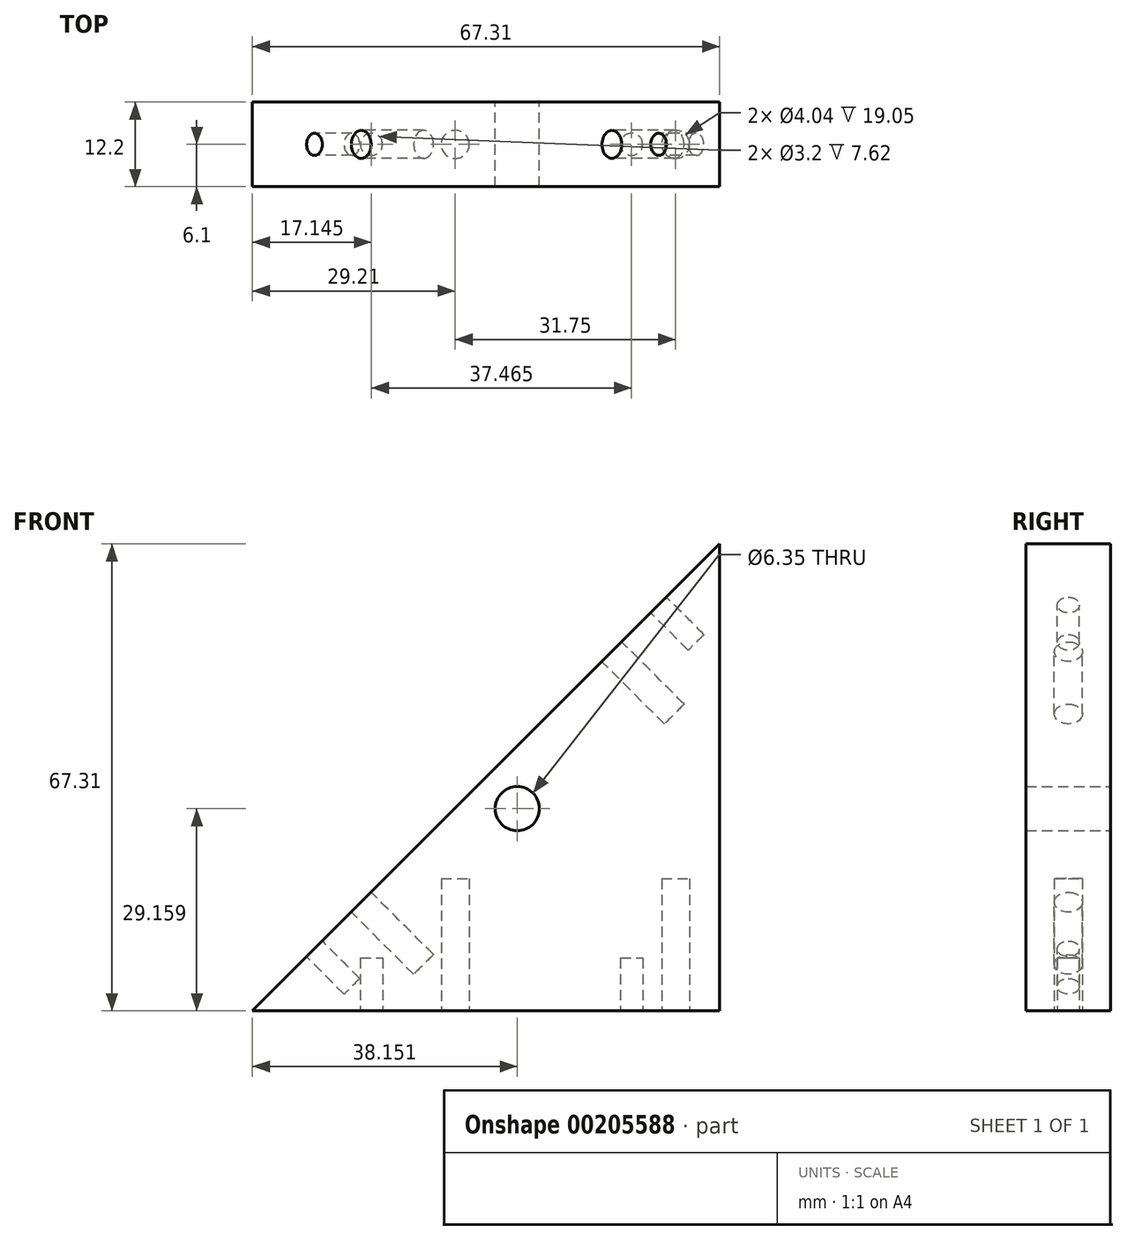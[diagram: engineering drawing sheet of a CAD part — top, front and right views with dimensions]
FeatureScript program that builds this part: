
annotation { "Feature Type Name" : "Feature", "Feature Type Description" : "" }
export const myFeature = defineFeature(function(context is Context, id is Id, definition is map)
    precondition{}
    {
        {
            var Q0;
            Q0=qCreatedBy(makeId("Front.planeOp"),FACE);
            var sketch = newSketch(context, id + "F0", { "sketchPlane" : qUnion([Q0])});
            skLineSegment(sketch, "E0", {"start": v(0, 0) * mm, "end": v(0, 67.31) * mm});
            skLineSegment(sketch, "E1", {"start": v(0, 67.31) * mm, "end": v(-67.31, 0) * mm});
            skLineSegment(sketch, "E2", {"start": v(-67.31, 0) * mm, "end": v(0, 0) * mm});
            skCircle(sketch, "E3", {"center": v(-29.16, 29.16) * mm, "radius": 3.18 * mm});
            skSolve(sketch);
        }
        {
            var Q0;
            Q0=qSketchRegion(id+"F0",true);
            extrude(context, id + "F1", {"entities" : qUnion([Q0]), "depth" : 12.2 * mm, "symmetric" : true});
        }
        {
            var Q0;
            Q0=makeQuery(id+"F1.opExtrude","SWEPT_FACE",FACE,{"disambiguationData":[OSD([sQuery(id+"F0.wireOp",EDGE,"E1")])]});
            var sketch = newSketch(context, id + "F2", { "sketchPlane" : qUnion([Q0])});
            skCircle(sketch, "E4", {"center": v(0, 35.15) * mm, "radius": 1.6 * mm});
            skCircle(sketch, "E5", {"center": v(0, -34.95) * mm, "radius": 1.6 * mm});
            skSolve(sketch);
        }
        {
            var Q0;
            Q0=qSketchRegion(id+"F2",true);
            extrude(context, id + "F3", {"entities" : qUnion([Q0]), "operationType" : NewBodyOperationType.REMOVE, "oppositeDirection" : true, "depth" : 7.62 * mm});
        }
        {
            var Q0;
            Q0=makeQuery(id+"F1.opExtrude","SWEPT_FACE",FACE,{"disambiguationData":[OSD([sQuery(id+"F0.wireOp",EDGE,"E1")])]});
            var sketch = newSketch(context, id + "F4", { "sketchPlane" : qUnion([Q0])});
            skCircle(sketch, "E6", {"center": v(0, 25.62) * mm, "radius": 2.02 * mm});
            skCircle(sketch, "E7", {"center": v(0, -25.43) * mm, "radius": 2.02 * mm});
            skSolve(sketch);
        }
        {
            var Q0;
            Q0=qSketchRegion(id+"F4",true);
            extrude(context, id + "F5", {"entities" : qUnion([Q0]), "operationType" : NewBodyOperationType.REMOVE, "oppositeDirection" : true, "depth" : 12.7 * mm});
        }
        {
            var Q0;
            Q0=makeQuery(id+"F1.opExtrude","SWEPT_FACE",FACE,{"disambiguationData":[OSD([sQuery(id+"F0.wireOp",EDGE,"E2")])]});
            var sketch = newSketch(context, id + "F6", { "sketchPlane" : qUnion([Q0])});
            skCircle(sketch, "E8", {"center": v(-6.35, 0) * mm, "radius": 2.02 * mm});
            skCircle(sketch, "E9", {"center": v(-38.1, 0) * mm, "radius": 2.02 * mm});
            skSolve(sketch);
        }
        {
            var Q0;
            Q0=qSketchRegion(id+"F6",true);
            extrude(context, id + "F7", {"entities" : qUnion([Q0]), "operationType" : NewBodyOperationType.REMOVE, "oppositeDirection" : true, "depth" : 19.05 * mm});
        }
        {
            var Q0;
            Q0=makeQuery(id+"F1.opExtrude","SWEPT_FACE",FACE,{"disambiguationData":[OSD([sQuery(id+"F0.wireOp",EDGE,"E2")])]});
            var sketch = newSketch(context, id + "F8", { "sketchPlane" : qUnion([Q0])});
            skCircle(sketch, "E10", {"center": v(-12.7, 0) * mm, "radius": 1.6 * mm});
            skCircle(sketch, "E11", {"center": v(-50.17, 0) * mm, "radius": 1.6 * mm});
            skSolve(sketch);
        }
        {
            var Q0;
            Q0=qSketchRegion(id+"F8",true);
            extrude(context, id + "F9", {"entities" : qUnion([Q0]), "operationType" : NewBodyOperationType.REMOVE, "oppositeDirection" : true, "depth" : 7.62 * mm});
        }
    });
